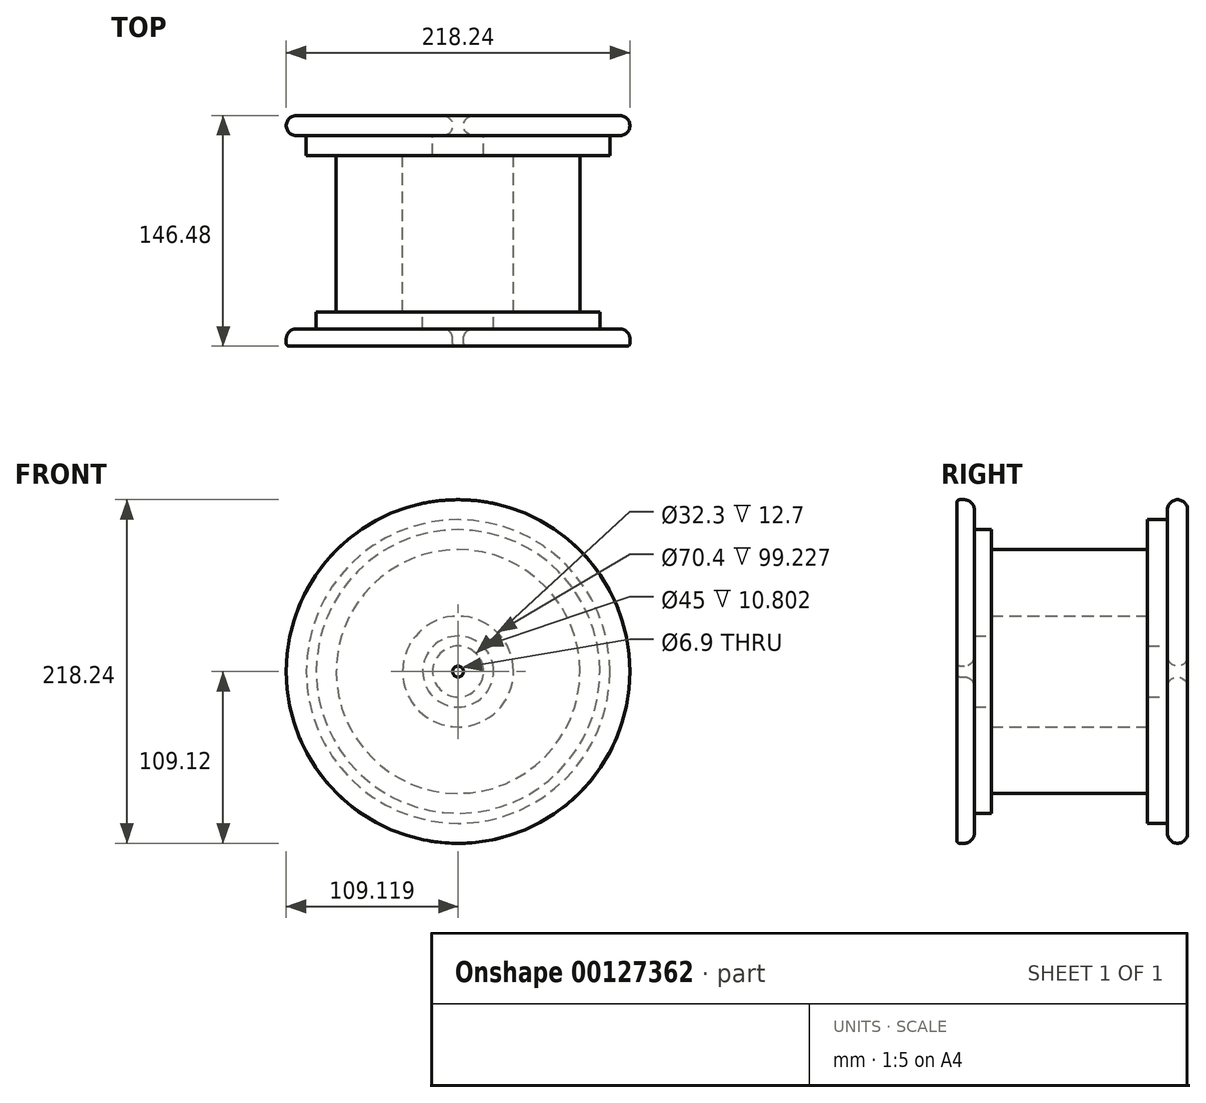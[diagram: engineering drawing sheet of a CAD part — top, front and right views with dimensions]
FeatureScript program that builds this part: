
annotation { "Feature Type Name" : "Feature", "Feature Type Description" : "" }
export const myFeature = defineFeature(function(context is Context, id is Id, definition is map)
    precondition{}
    {
        {
            var Q0;
            Q0=qCreatedBy(makeId("Top.planeOp"),FACE);
            var sketch = newSketch(context, id + "F0", { "sketchPlane" : qUnion([Q0])});
            skLineSegment(sketch, "E0.bottom", {"start": v(-25.34, 47.1) * mm, "end": v(16.83, 47.1) * mm});
            skLineSegment(sketch, "E0.top", {"start": v(-25.34, -52.13) * mm, "end": v(16.83, -52.13) * mm});
            skLineSegment(sketch, "E0.left", {"start": v(-25.34, 47.1) * mm, "end": v(-25.34, -52.13) * mm});
            skLineSegment(sketch, "E0.right", {"start": v(16.83, 47.1) * mm, "end": v(16.83, -52.13) * mm});
            skLineSegment(sketch, "E1.bottom", {"start": v(-38.04, -52.13) * mm, "end": v(29.53, -52.13) * mm});
            skLineSegment(sketch, "E1.top", {"start": v(-38.04, -62.93) * mm, "end": v(29.53, -62.93) * mm});
            skLineSegment(sketch, "E1.left", {"start": v(-38.04, -52.13) * mm, "end": v(-38.04, -62.93) * mm});
            skLineSegment(sketch, "E1.right", {"start": v(29.53, -52.13) * mm, "end": v(29.53, -62.93) * mm});
            skLineSegment(sketch, "E2.bottom", {"start": v(42.23, -62.93) * mm, "end": v(-50.74, -62.93) * mm});
            skLineSegment(sketch, "E2.top", {"start": v(46.86, -73.98) * mm, "end": v(-55.37, -73.98) * mm});
            skLineSegment(sketch, "E2.left", {"start": v(48.58, -69.28) * mm, "end": v(48.58, -72.26) * mm});
            skLineSegment(sketch, "E2.right", {"start": v(-57.1, -69.28) * mm, "end": v(-57.1, -72.26) * mm});
            skPoint(sketch, "E3.visualSharp", {"position": v(-57.1, -62.93) * mm});
            skArc(sketch, "E3.filletArc", {"start": v(-50.74, -62.93) * mm, "mid": v(-55.23, -64.79) * mm, "end": v(-57.1, -69.28) * mm});
            skPoint(sketch, "E4.visualSharp", {"position": v(48.58, -62.93) * mm});
            skArc(sketch, "E4.filletArc", {"start": v(48.58, -69.28) * mm, "mid": v(46.72, -64.79) * mm, "end": v(42.23, -62.93) * mm});
            skPoint(sketch, "E5.visualSharp", {"position": v(-57.1, -73.98) * mm});
            skArc(sketch, "E5.filletArc", {"start": v(-57.1, -72.26) * mm, "mid": v(-56.59, -73.48) * mm, "end": v(-55.37, -73.98) * mm});
            skPoint(sketch, "E6.visualSharp", {"position": v(48.58, -73.98) * mm});
            skArc(sketch, "E6.filletArc", {"start": v(46.86, -73.98) * mm, "mid": v(48.08, -73.48) * mm, "end": v(48.58, -72.26) * mm});
            skLineSegment(sketch, "E7.bottom", {"start": v(-44.4, 47.1) * mm, "end": v(35.88, 47.1) * mm});
            skLineSegment(sketch, "E7.top", {"start": v(-44.4, 59.8) * mm, "end": v(35.88, 59.8) * mm});
            skLineSegment(sketch, "E7.left", {"start": v(-44.4, 47.1) * mm, "end": v(-44.4, 59.8) * mm});
            skLineSegment(sketch, "E7.right", {"start": v(35.88, 47.1) * mm, "end": v(35.88, 59.8) * mm});
            skLineSegment(sketch, "E8.bottom", {"start": v(-50.74, 59.8) * mm, "end": v(42.23, 59.8) * mm});
            skLineSegment(sketch, "E8.top", {"start": v(-50.74, 72.5) * mm, "end": v(42.23, 72.5) * mm});
            skLineSegment(sketch, "E8.left", {"start": v(-57.1, 66.15) * mm, "end": v(-57.1, 66.15) * mm});
            skLineSegment(sketch, "E8.right", {"start": v(48.58, 66.15) * mm, "end": v(48.58, 66.15) * mm});
            skPoint(sketch, "E9.visualSharp", {"position": v(-57.1, 72.5) * mm});
            skArc(sketch, "E9.filletArc", {"start": v(-50.74, 72.5) * mm, "mid": v(-55.23, 70.64) * mm, "end": v(-57.1, 66.15) * mm});
            skPoint(sketch, "E10.visualSharp", {"position": v(-57.1, 59.8) * mm});
            skArc(sketch, "E10.filletArc", {"start": v(-57.1, 66.15) * mm, "mid": v(-55.23, 61.66) * mm, "end": v(-50.74, 59.8) * mm});
            skPoint(sketch, "E11.visualSharp", {"position": v(48.58, 72.5) * mm});
            skArc(sketch, "E11.filletArc", {"start": v(48.58, 66.15) * mm, "mid": v(46.72, 70.64) * mm, "end": v(42.23, 72.5) * mm});
            skPoint(sketch, "E12.visualSharp", {"position": v(48.58, 59.8) * mm});
            skArc(sketch, "E12.filletArc", {"start": v(42.23, 59.8) * mm, "mid": v(46.72, 61.66) * mm, "end": v(48.58, 66.15) * mm});
            skLineSegment(sketch, "E13", {"start": v(-60.54, 32.03) * mm, "end": v(-60.54, -17.2) * mm, "construction": true});
            skSolve(sketch);
        }
        {
            var Q0;
            Q0 = qSketchRegion(id + "F0", true);
            var Q1;
            Q1=sQuery(id+"F0.wireOp",EDGE,"E13");
            revolve(context, id + "F1", {"entities" : qUnion([Q0]), "axis" : qUnion([Q1]), "revolveType" : RevolveType.FULL});
        }
    });
